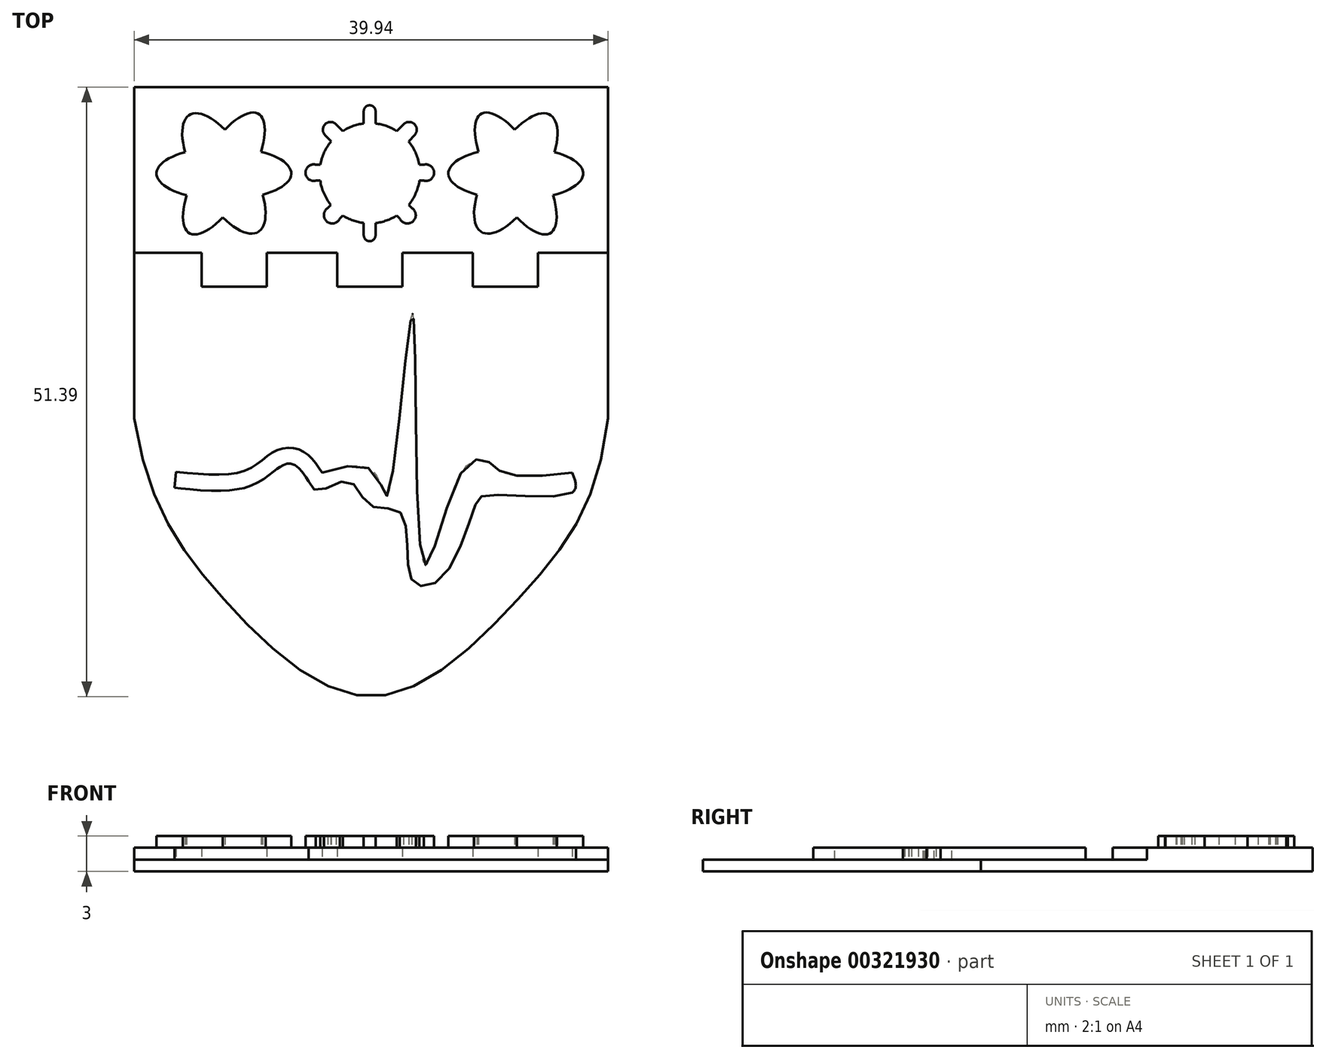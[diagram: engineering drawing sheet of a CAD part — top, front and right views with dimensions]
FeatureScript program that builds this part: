
annotation { "Feature Type Name" : "Feature", "Feature Type Description" : "" }
export const myFeature = defineFeature(function(context is Context, id is Id, definition is map)
    precondition{}
    {
        {
            var Q0;
            Q0=qCreatedBy(makeId("Top.planeOp"),FACE);
            var sketch = newSketch(context, id + "F0", { "sketchPlane" : qUnion([Q0])});
            skLineSegment(sketch, "E0", {"start": v(-63.4, 10.31) * mm, "end": v(-63.4, -41.75) * mm, "construction": true});
            skLineSegment(sketch, "E1", {"start": v(-103.4, 10.31) * mm, "end": v(-103.4, -41.75) * mm, "construction": true});
            skSolve(sketch);
        }
        {
            var Q0;
            Q0=qCreatedBy(makeId("Top.planeOp"),FACE);
            var sketch = newSketch(context, id + "F1", { "sketchPlane" : qUnion([Q0])});
            skLineSegment(sketch, "E2.bottom", {"start": v(-103.5, 9.92) * mm, "end": v(-63.55, 9.92) * mm});
            skLineSegment(sketch, "E2.top", {"start": v(-103.5, -18.02) * mm, "end": v(-63.55, -18.02) * mm});
            skLineSegment(sketch, "E2.left", {"start": v(-103.5, 9.92) * mm, "end": v(-103.5, -18.02) * mm});
            skLineSegment(sketch, "E2.right", {"start": v(-63.55, 9.92) * mm, "end": v(-63.55, -18.02) * mm});
            skLineSegment(sketch, "E3", {"start": v(-63.55, -18.02) * mm, "end": v(-63.55, -43.6) * mm, "construction": true});
            skLineSegment(sketch, "E4", {"start": v(-103.5, -18.02) * mm, "end": v(-103.5, -43.86) * mm, "construction": true});
            skLineSegment(sketch, "E5", {"start": v(-83.52, -18.02) * mm, "end": v(-83.52, -44.3) * mm, "construction": true});
            skLineSegment(sketch, "E6", {"start": v(-83.52, -18.02) * mm, "end": v(-103.5, -41.72) * mm, "construction": true});
            skLineSegment(sketch, "E7", {"start": v(-83.52, -18.02) * mm, "end": v(-63.55, -41.8) * mm, "construction": true});
            skLineSegment(sketch, "E8", {"start": v(-96.15, -33.01) * mm, "end": v(-70.94, -33.01) * mm, "construction": true});
            skLineSegment(sketch, "E9", {"start": v(-63.55, -25.47) * mm, "end": v(-103.5, -25.47) * mm, "construction": true});
            skFitSpline(sketch, "E10", {"points": [v(-103.5, -18.02) * mm, v(-96.15, -33.01) * mm, v(-83.52, -41.47) * mm, v(-70.94, -33.01) * mm, v(-63.55, -18.02) * mm], "startDerivative": vector(14.85, -87.28) * mm, "endDerivative": vector(10.03, 87.22) * mm});
            skSolve(sketch);
        }
        {
            var Q0;
            Q0=qSketchRegion(id+"F1",true);
            extrude(context, id + "F2", {"entities" : qUnion([Q0]), "depth" : 1 * mm});
        }
        {
            var Q0;
            Q0=makeQuery(id+"F2.opExtrude","CAP_FACE",FACE,{"disambiguationData":[OSD([sQuery(id+"F1.wireOp",EDGE,"E2.bottom"),sQuery(id+"F1.wireOp",EDGE,"E2.left"),sQuery(id+"F1.wireOp",EDGE,"E2.right"),sQuery(id+"F1.wireOp",EDGE,"E10")])],"isStart":false});
            var sketch = newSketch(context, id + "F3", { "sketchPlane" : qUnion([Q0])});
            skLineSegment(sketch, "E11.bottom", {"start": v(-63.55, 9.92) * mm, "end": v(-103.5, 9.92) * mm});
            skLineSegment(sketch, "E11.top", {"start": v(-63.55, -4.05) * mm, "end": v(-69.44, -4.05) * mm});
            skLineSegment(sketch, "E11.left", {"start": v(-63.55, 9.92) * mm, "end": v(-63.55, -4.05) * mm});
            skLineSegment(sketch, "E11.right", {"start": v(-103.5, 9.92) * mm, "end": v(-103.5, -4.05) * mm});
            skLineSegment(sketch, "E12.top", {"start": v(-97.82, -6.91) * mm, "end": v(-92.3, -6.91) * mm});
            skLineSegment(sketch, "E12.left", {"start": v(-97.82, -4.05) * mm, "end": v(-97.82, -6.91) * mm});
            skLineSegment(sketch, "E12.right", {"start": v(-92.3, -4.05) * mm, "end": v(-92.3, -6.91) * mm});
            skLineSegment(sketch, "E13.top", {"start": v(-86.38, -6.91) * mm, "end": v(-80.87, -6.91) * mm});
            skLineSegment(sketch, "E13.left", {"start": v(-86.38, -4.05) * mm, "end": v(-86.38, -6.91) * mm});
            skLineSegment(sketch, "E13.right", {"start": v(-80.87, -4.05) * mm, "end": v(-80.87, -6.91) * mm});
            skLineSegment(sketch, "E14.top", {"start": v(-74.95, -6.91) * mm, "end": v(-69.44, -6.91) * mm});
            skLineSegment(sketch, "E14.left", {"start": v(-74.95, -4.05) * mm, "end": v(-74.95, -6.91) * mm});
            skLineSegment(sketch, "E14.right", {"start": v(-69.44, -4.05) * mm, "end": v(-69.44, -6.91) * mm});
            skLineSegment(sketch, "E15.trimOffspring", {"start": v(-97.82, -4.05) * mm, "end": v(-103.5, -4.05) * mm});
            skLineSegment(sketch, "E16.trimOffspring", {"start": v(-86.38, -4.05) * mm, "end": v(-92.3, -4.05) * mm});
            skLineSegment(sketch, "E17.trimOffspring", {"start": v(-74.95, -4.05) * mm, "end": v(-80.87, -4.05) * mm});
            skFitSpline(sketch, "E18", {"points": [v(-99.96, -22.53) * mm, v(-94.26, -22.46) * mm, v(-92.08, -21.05) * mm, v(-90.35, -20.48) * mm, v(-88.8, -21.12) * mm, v(-87.66, -22.6) * mm], "startDerivative": vector(21.7, -2.11) * mm, "endDerivative": vector(6.06, -9.47) * mm});
            skFitSpline(sketch, "E19", {"points": [v(-87.66, -22.6) * mm, v(-83.23, -22.6) * mm, v(-82.14, -24.52) * mm, v(-80.03, -9.2) * mm, v(-79.07, -30.28) * mm, v(-75.93, -22.6) * mm, v(-73.8, -21.57) * mm, v(-72.4, -22.6) * mm, v(-66.57, -22.6) * mm], "startDerivative": vector(50.98, 15.32) * mm, "endDerivative": vector(58.72, 6.42) * mm});
            skFitSpline(sketch, "E20.0", {"points": [v(-100.1, -23.87) * mm, v(-99.64, -23.91) * mm, v(-98.73, -24) * mm, v(-97.36, -24.1) * mm, v(-96.25, -24.12) * mm, v(-95.39, -24.06) * mm, v(-94.76, -23.98) * mm, v(-94.14, -23.85) * mm, v(-93.53, -23.64) * mm, v(-93, -23.38) * mm, v(-92.55, -23.1) * mm, v(-92.16, -22.81) * mm, v(-91.83, -22.55) * mm, v(-91.6, -22.37) * mm, v(-91.43, -22.24) * mm, v(-91.32, -22.17) * mm, v(-91.22, -22.1) * mm, v(-91.08, -22.02) * mm, v(-90.9, -21.93) * mm, v(-90.73, -21.87) * mm, v(-90.57, -21.83) * mm, v(-90.44, -21.82) * mm, v(-90.3, -21.83) * mm, v(-90.06, -21.89) * mm, v(-89.8, -22.04) * mm, v(-89.62, -22.2) * mm, v(-89.42, -22.4) * mm, v(-89.15, -22.75) * mm, v(-88.92, -23.12) * mm, v(-88.79, -23.32) * mm]});
            skFitSpline(sketch, "E21", {"points": [v(-88.79, -23.32) * mm, v(-88, -24.1) * mm, v(-85.36, -23.32) * mm, v(-83.64, -25.33) * mm, v(-81.2, -25.8) * mm, v(-80.48, -29.1) * mm, v(-79.8, -31.94) * mm, v(-77.5, -31.4) * mm, v(-74.78, -25.42) * mm, v(-73.7, -24.47) * mm, v(-66.57, -24.26) * mm, v(-66.57, -22.6) * mm], "startDerivative": vector(9.8, -20.76) * mm, "endDerivative": vector(-11.42, 28.85) * mm});
            skLineSegment(sketch, "E22", {"start": v(-66.57, -22.6) * mm, "end": v(-66.57, -24.26) * mm});
            skLineSegment(sketch, "E23", {"start": v(-99.96, -22.53) * mm, "end": v(-100.1, -23.87) * mm});
            skSolve(sketch);
        }
        {
            var Q0;
            Q0 = qSketchRegion(id + "F3", true);
            extrude(context, id + "F4", {"entities" : qUnion([Q0]), "operationType" : NewBodyOperationType.ADD, "depth" : 1 * mm});
        }
        {
            var Q0;
            Q0=makeQuery(id+"F4.opExtrude","CAP_FACE",FACE,{"disambiguationData":[OSD([sQuery(id+"F3.wireOp",EDGE,"E11.bottom"),sQuery(id+"F3.wireOp",EDGE,"E11.top"),sQuery(id+"F3.wireOp",EDGE,"E11.left"),sQuery(id+"F3.wireOp",EDGE,"E11.right"),sQuery(id+"F3.wireOp",EDGE,"E12.top"),sQuery(id+"F3.wireOp",EDGE,"E12.left"),sQuery(id+"F3.wireOp",EDGE,"E12.right"),sQuery(id+"F3.wireOp",EDGE,"E13.top"),sQuery(id+"F3.wireOp",EDGE,"E13.left"),sQuery(id+"F3.wireOp",EDGE,"E13.right"),sQuery(id+"F3.wireOp",EDGE,"E14.top"),sQuery(id+"F3.wireOp",EDGE,"E14.left"),sQuery(id+"F3.wireOp",EDGE,"E14.right"),sQuery(id+"F3.wireOp",EDGE,"E15.trimOffspring"),sQuery(id+"F3.wireOp",EDGE,"E16.trimOffspring"),sQuery(id+"F3.wireOp",EDGE,"E17.trimOffspring")])],"isStart":false});
            var sketch = newSketch(context, id + "F5", { "sketchPlane" : qUnion([Q0])});
            skLineSegment(sketch, "E24", {"start": v(-83.63, -6.91) * mm, "end": v(-83.63, 6.89) * mm, "construction": true});
            skArc(sketch, "E25", {"start": v(-84.14, 6.86) * mm, "mid": v(-85.06, 6.64) * mm, "end": v(-85.9, 6.22) * mm});
            skLineSegment(sketch, "E26", {"start": v(-87.8, 3.38) * mm, "end": v(-88.54, 3.38) * mm});
            skLineSegment(sketch, "E27", {"start": v(-87.8, 2.04) * mm, "end": v(-88.54, 2.04) * mm});
            skLineSegment(sketch, "E28", {"start": v(-86.91, 0) * mm, "end": v(-87.4, -0.52) * mm});
            skLineSegment(sketch, "E29", {"start": v(-85.9, -0.9) * mm, "end": v(-86.46, -1.5) * mm});
            skLineSegment(sketch, "E30", {"start": v(-86.9, 5.34) * mm, "end": v(-87.4, 5.9) * mm});
            skLineSegment(sketch, "E31", {"start": v(-85.9, 6.22) * mm, "end": v(-86.46, 6.78) * mm});
            skArc(sketch, "E32", {"start": v(-86.46, 6.78) * mm, "mid": v(-87.38, 6.81) * mm, "end": v(-87.4, 5.9) * mm});
            skPoint(sketch, "E32.third.point", {"position": v(-87.4, 6.78) * mm});
            skArc(sketch, "E33", {"start": v(-88.18, 3.38) * mm, "mid": v(-89.05, 2.71) * mm, "end": v(-88.18, 2.04) * mm});
            skPoint(sketch, "E33.third.point", {"position": v(-88.18, 2.04) * mm});
            skArc(sketch, "E34", {"start": v(-87.16, -0.26) * mm, "mid": v(-87.26, -1.4) * mm, "end": v(-86.15, -1.16) * mm});
            skPoint(sketch, "E34.third.point", {"position": v(-87.16, -0.26) * mm});
            skArc(sketch, "E35.trimOffspring", {"start": v(-86.9, 5.34) * mm, "mid": v(-87.47, 4.42) * mm, "end": v(-87.8, 3.38) * mm});
            skArc(sketch, "E36.trimOffspring", {"start": v(-87.8, 2.04) * mm, "mid": v(-87.5, 0.96) * mm, "end": v(-86.91, 0) * mm});
            skArc(sketch, "E37.trimOffspring", {"start": v(-85.9, -0.9) * mm, "mid": v(-83.63, -1.56) * mm, "end": v(-81.36, -0.9) * mm});
            skEllipticalArc(sketch, "E38", {});
            skEllipticalArc(sketch, "E39", {});
            skEllipticalArc(sketch, "E40", {});
            skEllipticalArc(sketch, "E41.trimOffspring", {});
            skEllipticalArc(sketch, "E42.trimOffspring", {});
            skEllipticalArc(sketch, "E43.trimOffspring", {});
            skLineSegment(sketch, "E44.MirrorCS", {"start": v(-80.34, 0) * mm, "end": v(-79.84, -0.52) * mm});
            skLineSegment(sketch, "E45.MirrorCS", {"start": v(-79.46, 3.38) * mm, "end": v(-78.71, 3.38) * mm});
            skLineSegment(sketch, "E46.MirrorCS", {"start": v(-79.45, 2.04) * mm, "end": v(-78.71, 2.04) * mm});
            skLineSegment(sketch, "E47.MirrorCS", {"start": v(-80.36, 5.34) * mm, "end": v(-79.84, 5.9) * mm});
            skLineSegment(sketch, "E48.MirrorCS", {"start": v(-81.35, 6.22) * mm, "end": v(-80.8, 6.78) * mm});
            skLineSegment(sketch, "E49.MirrorCS", {"start": v(-81.36, -0.9) * mm, "end": v(-80.8, -1.5) * mm});
            skArc(sketch, "E50.MirrorCS", {"start": v(-80.8, 6.78) * mm, "mid": v(-79.88, 6.81) * mm, "end": v(-79.84, 5.9) * mm});
            skPoint(sketch, "E51.MirrorP", {"position": v(-80.1, -0.26) * mm});
            skPoint(sketch, "E52.MirrorP", {"position": v(-79.08, 2.04) * mm});
            skPoint(sketch, "E53.MirrorP", {"position": v(-79.84, 6.78) * mm});
            skArc(sketch, "E54.MirrorCS", {"start": v(-79.45, 2.04) * mm, "mid": v(-79.76, 0.96) * mm, "end": v(-80.34, 0) * mm});
            skArc(sketch, "E55.MirrorCS", {"start": v(-80.36, 5.34) * mm, "mid": v(-79.78, 4.42) * mm, "end": v(-79.46, 3.38) * mm});
            skArc(sketch, "E56.MirrorCS", {"start": v(-80.1, -0.26) * mm, "mid": v(-80, -1.4) * mm, "end": v(-81.1, -1.16) * mm});
            skArc(sketch, "E57.MirrorCS", {"start": v(-79.08, 3.38) * mm, "mid": v(-78.2, 2.71) * mm, "end": v(-79.08, 2.04) * mm});
            skArc(sketch, "E58.MirrorCS", {"start": v(-81.36, -0.9) * mm, "mid": v(-82.22, -1.32) * mm, "end": v(-83.15, -1.54) * mm});
            skArc(sketch, "E59.MirrorCS", {"start": v(-83.15, 6.86) * mm, "mid": v(-82.21, 6.65) * mm, "end": v(-81.35, 6.22) * mm});
            skLineSegment(sketch, "E60.trimOffspring", {"start": v(-83.63, 6.89) * mm, "end": v(-83.63, 9.92) * mm, "construction": true});
            skLineSegment(sketch, "E61", {"start": v(-83.63, 6.89) * mm, "end": v(-83.63, 6.89) * mm});
            skEllipticalArc(sketch, "E62.MirrorCS", {});
            skEllipticalArc(sketch, "E63.MirrorCS", {});
            skEllipticalArc(sketch, "E64.MirrorCS", {});
            skEllipticalArc(sketch, "E65.MirrorCS", {});
            skEllipticalArc(sketch, "E66.MirrorCS", {});
            skEllipticalArc(sketch, "E67.MirrorCS", {});
            skLineSegment(sketch, "E68", {"start": v(-84.14, -1.53) * mm, "end": v(-84.14, -2.6) * mm});
            skLineSegment(sketch, "E69", {"start": v(-83.15, -1.54) * mm, "end": v(-83.15, -2.62) * mm});
            skArc(sketch, "E70", {"start": v(-84.14, -2.55) * mm, "mid": v(-83.63, -3.07) * mm, "end": v(-83.15, -2.52) * mm});
            skPoint(sketch, "E70.third.point", {"position": v(-83.63, -2.08) * mm});
            skPoint(sketch, "E70.third.point.positionSnap0", {"position": v(-83.15, -2.08) * mm});
            skLineSegment(sketch, "E71", {"start": v(-83.63, 2.66) * mm, "end": v(-92.32, 2.66) * mm, "construction": true});
            skArc(sketch, "E72.MirrorCS", {"start": v(-84.14, 7.88) * mm, "mid": v(-83.63, 8.4) * mm, "end": v(-83.15, 7.85) * mm});
            skPoint(sketch, "E73.MirrorP", {"position": v(-83.15, 7.4) * mm});
            skPoint(sketch, "E74.MirrorP", {"position": v(-83.63, 7.4) * mm});
            skLineSegment(sketch, "E75.MirrorCS", {"start": v(-84.14, 6.86) * mm, "end": v(-84.14, 7.92) * mm});
            skLineSegment(sketch, "E76.MirrorCS", {"start": v(-83.15, 6.86) * mm, "end": v(-83.15, 7.95) * mm});
            skArc(sketch, "E77.trimOffspring", {"start": v(-85.9, 6.22) * mm, "mid": v(-85.06, 6.64) * mm, "end": v(-84.14, 6.86) * mm});
            skArc(sketch, "E78.trimOffspring", {"start": v(-87.8, 3.38) * mm, "mid": v(-87.47, 4.42) * mm, "end": v(-86.9, 5.34) * mm});
            skArc(sketch, "E79.trimOffspring", {"start": v(-86.91, 0) * mm, "mid": v(-87.5, 0.96) * mm, "end": v(-87.8, 2.04) * mm});
            skArc(sketch, "E80.trimOffspring", {"start": v(-84.14, -1.53) * mm, "mid": v(-85.05, -1.32) * mm, "end": v(-85.9, -0.9) * mm});
            skArc(sketch, "E81.trimOffspring", {"start": v(-80.34, 0) * mm, "mid": v(-79.76, 0.96) * mm, "end": v(-79.45, 2.04) * mm});
            skArc(sketch, "E82.trimOffspring", {"start": v(-79.46, 3.38) * mm, "mid": v(-79.78, 4.42) * mm, "end": v(-80.36, 5.34) * mm});
            skArc(sketch, "E83.trimOffspring", {"start": v(-81.35, 6.22) * mm, "mid": v(-82.21, 6.65) * mm, "end": v(-83.15, 6.86) * mm});
            skPoint(sketch, "E84.orphan", {"position": v(-83.63, 6.89) * mm});
            const initialGuessF5  = {"E38": [-0.09593164920806885, 0.002646032255142927, -1, 0, 0.005682237446308136, 0.0021987649877151312, 5.326754780961285, 0.9854542017602633], "E39": [-0.09593164920806885, 0.002646032255142927, 0.5014232729867973, 0.8652021158707415, 0.005808463961423635, 0.0021418621338835393, 2.1459957754750296, 4.120553612900027], "E40": [-0.09593164920806885, 0.002646032255142927, 0.5041813261780044, -0.8635978174667817, 0.005720061882453156, 0.0023208167371799628, 2.153396001982681, 4.118041069374778], "E41.trimOffspring": [-0.09593164920806885, 0.002646032255142927, 0.5014232729867973, 0.8652021158707415, 0.005808463961423635, 0.0021418621338835393, 5.287588429064824, 0.978960959310234], "E42.trimOffspring": [-0.09593164920806885, 0.002646032255142927, 0.5041813261780044, -0.8635978174667817, 0.005720061882453156, 0.0023208167371799628, 5.294988655572474, 0.9764484157849856], "E43.trimOffspring": [-0.09593164920806885, 0.002646032255142927, -1, 0, 0.005682237446308136, 0.0021987649877151312, 2.185162127371492, 4.127046855350056], "E62.MirrorCS": [-0.07132328301668167, 0.002646032255142927, -0.5014232729867973, 0.8652021158707415, 0.005808463961423635, 0.0021418621338835393, 5.3042243478693525, 0.9955968781147622], "E63.MirrorCS": [-0.07132328301668167, 0.002646032255142927, 1, 0, 0.005682237446308136, 0.0021987649877151312, 2.1561384518295306, 4.098023179808095], "E64.MirrorCS": [-0.07132328301668167, 0.002646032255142927, -0.5041813261780044, -0.8635978174667817, 0.005720061882453156, 0.0023208167371799628, 5.3067368913946, 0.9881966516071126], "E65.MirrorCS": [-0.07132328301668167, 0.002646032255142927, -0.5014232729867973, 0.8652021158707415, 0.005808463961423635, 0.0021418621338835393, 2.1626316942795594, 4.137189531704557], "E66.MirrorCS": [-0.07132328301668167, 0.002646032255142927, 1, 0, 0.005682237446308136, 0.0021987649877151312, 5.297731105419323, 0.956430526218301], "E67.MirrorCS": [-0.07132328301668167, 0.002646032255142927, -0.5041813261780044, -0.8635978174667817, 0.005720061882453156, 0.0023208167371799628, 2.1651442378048085, 4.129789305196905]};
            skSetInitialGuess(sketch, initialGuessF5);
            skSolve(sketch);
        }
        {
            var Q0;
            Q0 = qSketchRegion(id + "F5", true);
            extrude(context, id + "F6", {"entities" : qUnion([Q0]), "operationType" : NewBodyOperationType.ADD, "depth" : 1 * mm});
        }
    });
